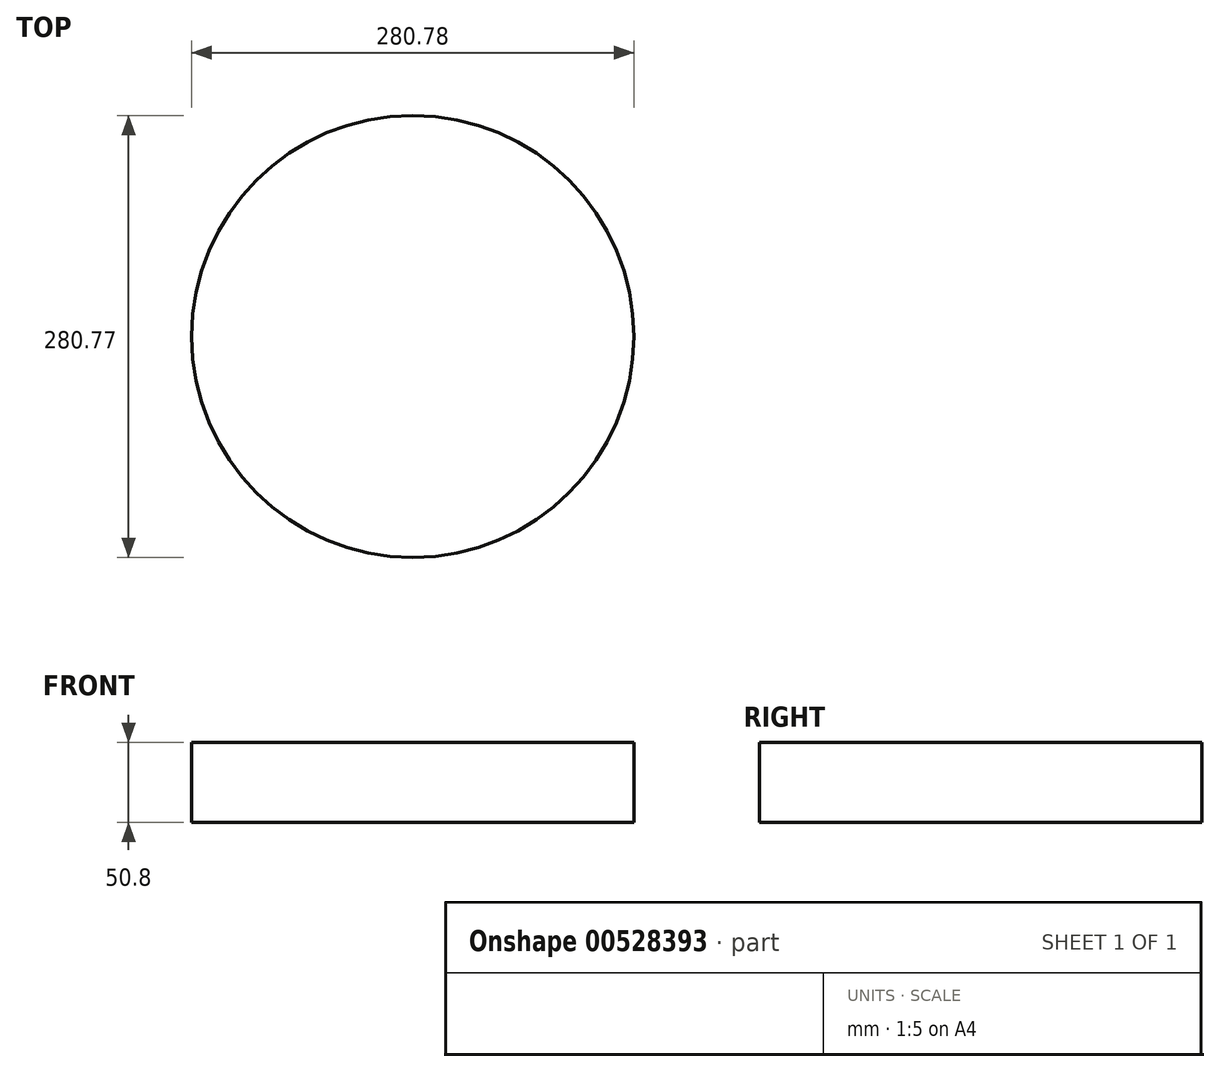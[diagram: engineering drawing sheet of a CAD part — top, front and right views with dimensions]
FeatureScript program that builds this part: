
annotation { "Feature Type Name" : "Feature", "Feature Type Description" : "" }
export const myFeature = defineFeature(function(context is Context, id is Id, definition is map)
    precondition{}
    {
        {
            var Q0;
            Q0=qCreatedBy(makeId("Top.planeOp"),FACE);
            var sketch = newSketch(context, id + "F0", { "sketchPlane" : qUnion([Q0])});
            skCircle(sketch, "E0", {"center": v(-13.56, -10.95) * mm, "radius": 140.39 * mm});
            skSolve(sketch);
        }
        {
            var Q0;
            Q0=sQuery(id+"F0.wireOp",EDGE,"E0");
            extrude(context, id + "F1", {"bodyType" : ToolBodyType.SURFACE, "surfaceEntities" : qUnion([Q0]), "depth" : 50.8 * mm, "offsetDistance" : 25.4 * mm});
        }
    });
